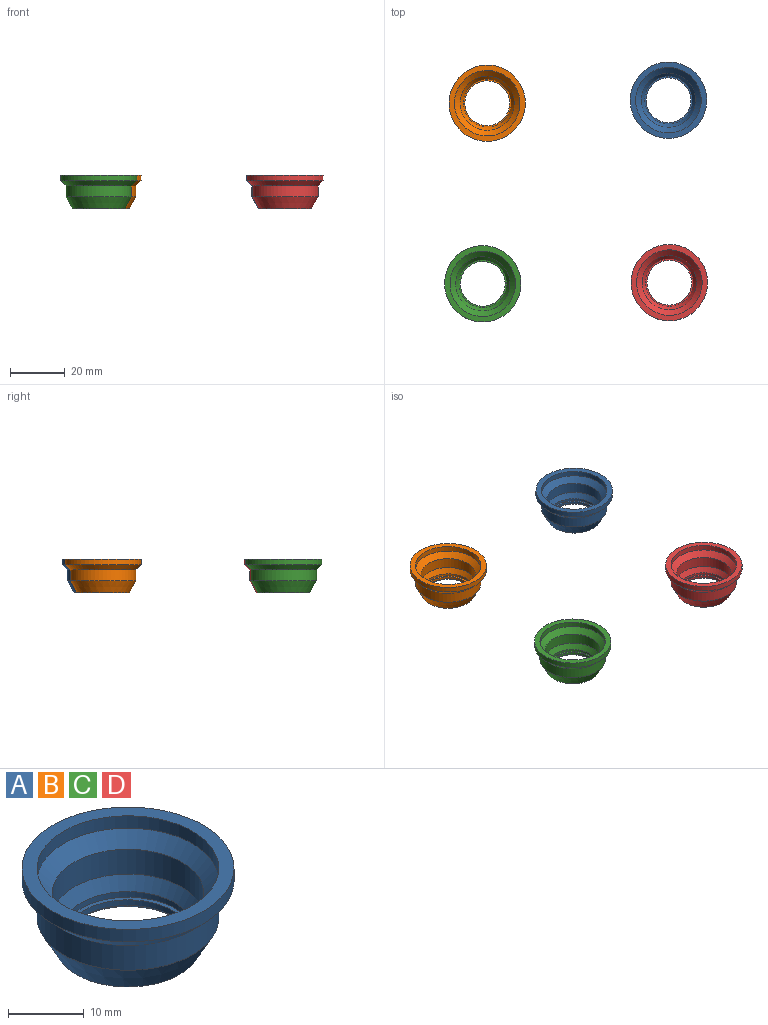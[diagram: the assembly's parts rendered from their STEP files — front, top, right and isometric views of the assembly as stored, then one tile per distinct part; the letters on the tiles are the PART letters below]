
ASSEMBLY  parts=4 mates=3
PART A: 14 faces, bbox 28x28x12.4 mm
  f0: plane 17.6x17.6mm, normal (0,0,1), area 32mm2, adj f1,f12
  f1: cylinder r=8.2mm len=16.4mm, axis (0,0,-1), area 46.4mm2, adj f0,f13
  f2: plane 19.2x19.2mm, normal (0,0,-1), area 46.2mm2, adj f3,f13
  f3: cone r=9.6mm half-angle=28.6deg, axis (0,0,1), area 340.1mm2, adj f2,f4
  f4: cylinder r=12mm len=24mm, axis (0,0,-1), area 301.6mm2, adj f3,f5
  f5: cone r=12mm half-angle=45deg, axis (0,0,1), area 231mm2, adj f4,f6
  f6: cylinder r=14mm len=28mm, axis (0,0,-1), area 175.9mm2, adj f5,f7
  f7: plane 28x28mm, normal (0,0,1), area 163.4mm2, adj f6,f8
  f8: cylinder r=12mm len=24mm, axis (0,0,-1), area 150.8mm2, adj f7,f9
  f9: cone r=10mm half-angle=45deg, axis (0,0,1), area 195.5mm2, adj f8,f10
  f10: cylinder r=10mm len=20mm, axis (0,0,-1), area 251.3mm2, adj f9,f11
  f11: cone r=8.8mm half-angle=31deg, axis (0,0,1), area 137.8mm2, adj f10,f12
  f12: cylinder r=8.8mm len=17.6mm, axis (0,0,-1), area 49.8mm2, adj f0,f11
  f13: cone r=8.2mm half-angle=45deg, axis (0,0,-1), area 45.3mm2, adj f1,f2
PART B: same geometry as A
PART C: same geometry as A
PART D: same geometry as A
PLACE A t=(33.97,33.75,-15.92)mm
PLACE B t=(-32.42,32.64,-15.92)mm
PLACE C t=(-34.06,-33.51,-15.92)mm
PLACE D t=(34.29,-33.09,-15.92)mm
MATE planar D.f1 <-> C.f1  axis (0,0,-1) through (34.29,-33.09,-15.92)mm
MATE planar A.f1 <-> B.f1  axis (0,0,-1) through (33.97,33.75,-15.92)mm
MATE planar B.f1 <-> C.f1  axis (0,0,-1) through (-32.42,32.64,-15.92)mm
